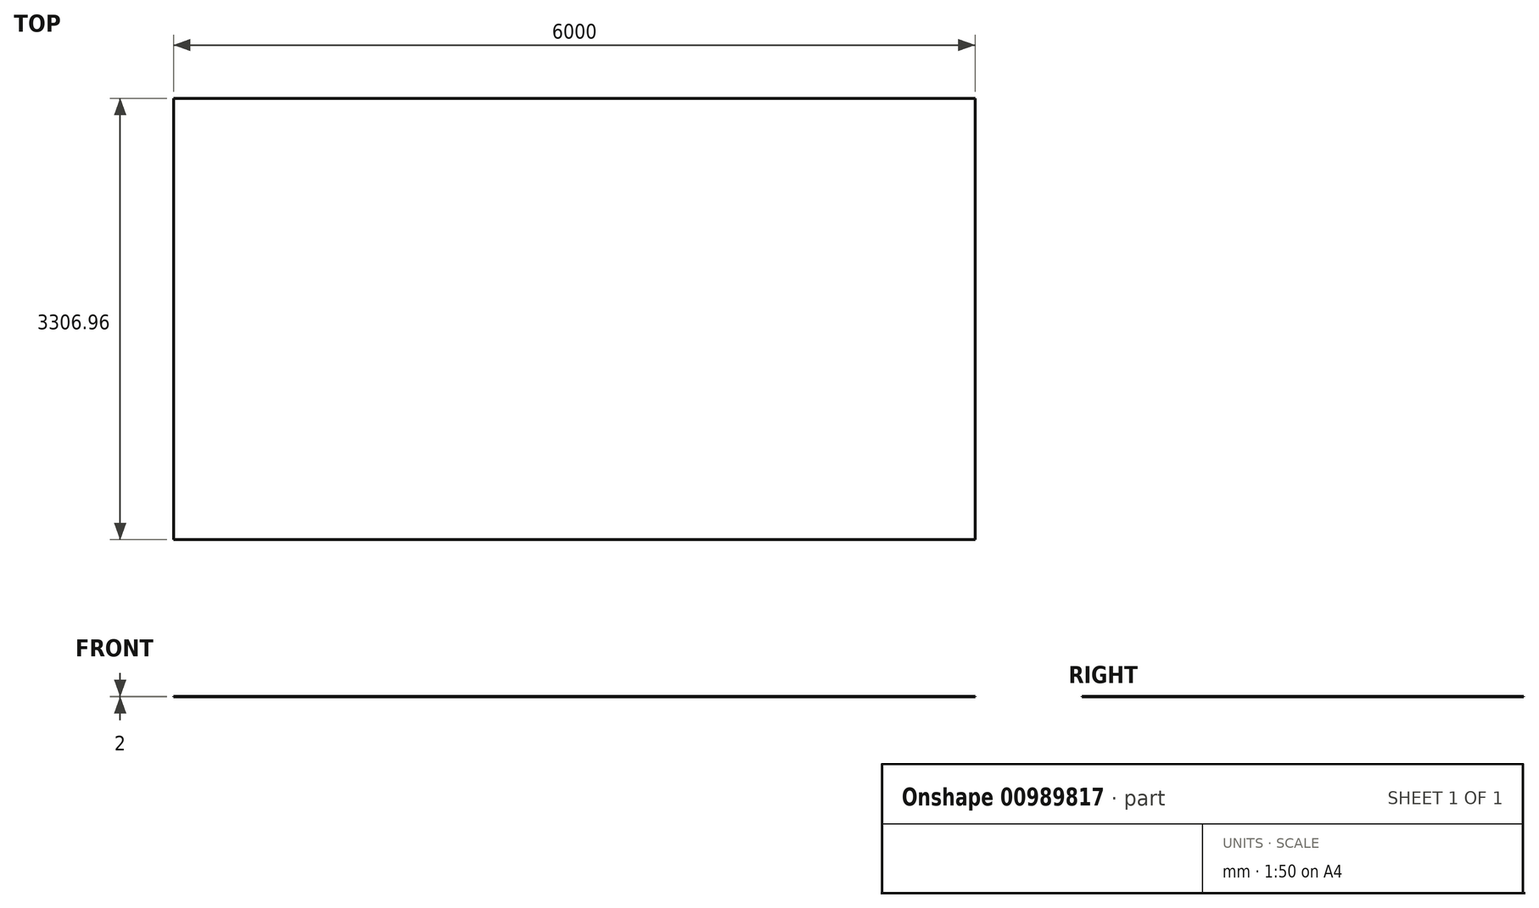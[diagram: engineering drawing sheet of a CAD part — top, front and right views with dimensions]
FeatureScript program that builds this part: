
annotation { "Feature Type Name" : "Feature", "Feature Type Description" : "" }
export const myFeature = defineFeature(function(context is Context, id is Id, definition is map)
    precondition{}
    {
        {
            var Q0;
            Q0=qCreatedBy(makeId("Top.planeOp"),FACE);
            var sketch = newSketch(context, id + "F0", { "sketchPlane" : qUnion([Q0])});
            skLineSegment(sketch, "E0.bottom", {"start": v(-2999.06, 1646.08) * mm, "end": v(3000.94, 1646.08) * mm});
            skLineSegment(sketch, "E0.top", {"start": v(-2999.06, -1660.88) * mm, "end": v(3000.94, -1660.88) * mm});
            skLineSegment(sketch, "E0.left", {"start": v(-2999.06, 1646.08) * mm, "end": v(-2999.06, -1660.88) * mm});
            skLineSegment(sketch, "E0.right", {"start": v(3000.94, 1646.08) * mm, "end": v(3000.94, -1660.88) * mm});
            skSolve(sketch);
        }
        {
            var Q0;
            Q0=makeQuery(id+"F0.imprint","IMPRINT",FACE,{"disambiguationData":[TD([[makeQuery(id+"F0.imprint","IMPRINT",EDGE,{"derivedFrom":sQuery(id+"F0.wireOp",EDGE,"E0.bottom")}),-1.0]])]});
            extrude(context, id + "F1", {"entities" : qUnion([Q0]), "depth" : 2 * mm, "offsetDistance" : 25 * mm});
        }
    });
